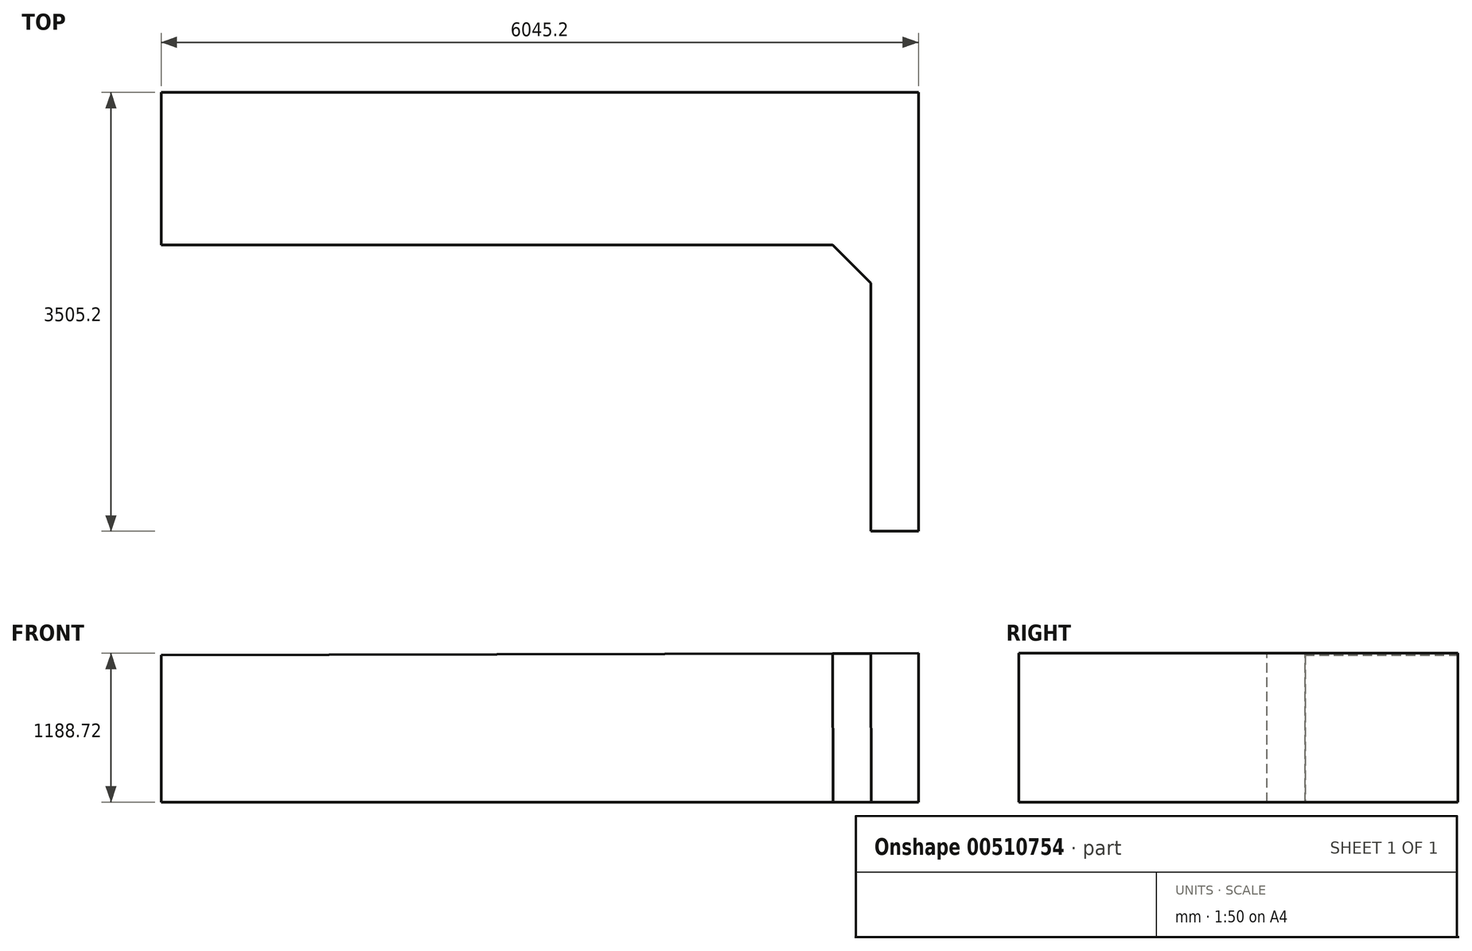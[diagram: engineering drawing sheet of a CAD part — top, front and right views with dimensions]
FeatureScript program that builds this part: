
annotation { "Feature Type Name" : "Feature", "Feature Type Description" : "" }
export const myFeature = defineFeature(function(context is Context, id is Id, definition is map)
    precondition{}
    {
        {
            var Q0;
            Q0=qCreatedBy(makeId("Right.planeOp"),FACE);
            var sketch = newSketch(context, id + "F0", { "sketchPlane" : qUnion([Q0])});
            skLineSegment(sketch, "E0.bottom", {"start": v(0, 295.66) * mm, "end": v(-3505.2, 295.66) * mm});
            skLineSegment(sketch, "E0.top", {"start": v(0, 1484.38) * mm, "end": v(-3505.2, 1484.38) * mm});
            skLineSegment(sketch, "E0.left", {"start": v(0, 295.66) * mm, "end": v(0, 1484.38) * mm});
            skLineSegment(sketch, "E0.right", {"start": v(-3505.2, 295.66) * mm, "end": v(-3505.2, 1484.38) * mm});
            skSolve(sketch);
        }
        {
            var Q0;
            Q0=qCreatedBy(makeId("Right.planeOp"),FACE);
            cPlane(context, id + "F1", {"entities" : qUnion([Q0]), "cplaneType" : CPlaneType.OFFSET, "offset" : 12115.8 * mm, "oppositeDirection" : true, "width" : 152.4 * mm, "height" : 152.4 * mm});
        }
        {
            var Q0;
            Q0=qCreatedBy(id+"F1.planeOp",FACE);
            var sketch = newSketch(context, id + "F2", { "sketchPlane" : qUnion([Q0])});
            skLineSegment(sketch, "E1.bottom", {"start": v(0, 295.66) * mm, "end": v(-3505.2, 295.66) * mm});
            skLineSegment(sketch, "E1.top", {"start": v(0, 1450.85) * mm, "end": v(-3505.2, 1450.85) * mm});
            skLineSegment(sketch, "E1.left", {"start": v(0, 295.66) * mm, "end": v(0, 1450.85) * mm});
            skLineSegment(sketch, "E1.right", {"start": v(-3505.2, 295.66) * mm, "end": v(-3505.2, 1450.85) * mm});
            skSolve(sketch);
        }
        {
            var Q0;
            Q0=makeQuery(id+"F0.imprint","IMPRINT",FACE,{"disambiguationData":[TD([[makeQuery(id+"F0.imprint","IMPRINT",EDGE,{"derivedFrom":sQuery(id+"F0.wireOp",EDGE,"E0.bottom")}),-1.0]])]});
            var Q1;
            Q1=makeQuery(id+"F2.imprint","IMPRINT",FACE,{"disambiguationData":[TD([[makeQuery(id+"F2.imprint","IMPRINT",EDGE,{"derivedFrom":sQuery(id+"F2.wireOp",EDGE,"E1.bottom")}),-1.0]])]});
            loft(context, id + "F3", {"sheetProfilesArray" : [{ "sheetProfileEntities" : qUnion([Q0]) }, { "sheetProfileEntities" : qUnion([Q1]) }]});
        }
        {
            var Q0;
            Q0=makeQuery(id+"F3.opLoft","SWEPT_FACE",FACE,{"disambiguationData":[OSD([sQuery(id+"F0.wireOp",EDGE,"E0.top"),sQuery(id+"F0.wireOp",EDGE,"E0.left"),sQuery(id+"F0.wireOp",EDGE,"E0.right"),sQuery(id+"F2.wireOp",EDGE,"E1.top"),sQuery(id+"F2.wireOp",EDGE,"E1.left"),sQuery(id+"F2.wireOp",EDGE,"E1.right")])]});
            var sketch = newSketch(context, id + "F4", { "sketchPlane" : qUnion([Q0])});
            skLineSegment(sketch, "E2", {"start": v(-11730.74, -3505.2) * mm, "end": v(-11730.74, -1524) * mm});
            skLineSegment(sketch, "E3", {"start": v(-11730.74, -1524) * mm, "end": v(-11425.94, -1219.2) * mm});
            skLineSegment(sketch, "E4", {"start": v(-11425.94, -1219.2) * mm, "end": v(-681.7, -1219.2) * mm});
            skLineSegment(sketch, "E5", {"start": v(-681.7, -1219.2) * mm, "end": v(-376.9, -1524) * mm});
            skLineSegment(sketch, "E6", {"start": v(-376.9, -1524) * mm, "end": v(-376.9, -3505.2) * mm});
            skLineSegment(sketch, "E7", {"start": v(-376.9, -3505.2) * mm, "end": v(-11730.74, -3505.2) * mm});
            skSolve(sketch);
        }
        {
            var Q0;
            Q0 = qSketchRegion(id + "F4", true);
            extrude(context, id + "F5", {"entities" : qUnion([Q0]), "operationType" : NewBodyOperationType.REMOVE, "endBound" : BoundingType.UP_TO_NEXT, "oppositeDirection" : true, "depth" : 30.48 * mm});
        }
        {
            var Q0;
            Q0=qCreatedBy(makeId("Right.planeOp"),FACE);
            cPlane(context, id + "F6", {"entities" : qUnion([Q0]), "cplaneType" : CPlaneType.OFFSET, "offset" : 6045.2 * mm, "oppositeDirection" : true, "width" : 152.4 * mm, "height" : 152.4 * mm});
        }
        {
            var Q0;
            Q0=qCreatedBy(id+"F6.planeOp",FACE);
            var sketch = newSketch(context, id + "F7", { "sketchPlane" : qUnion([Q0])});
            skLineSegment(sketch, "E8.bottom", {"start": v(0, 0) * mm, "end": v(-3505.2, 0) * mm});
            skLineSegment(sketch, "E8.top", {"start": v(0, 1828.8) * mm, "end": v(-3505.2, 1828.8) * mm});
            skLineSegment(sketch, "E8.left", {"start": v(0, 0) * mm, "end": v(0, 1828.8) * mm});
            skLineSegment(sketch, "E8.right", {"start": v(-3505.2, 0) * mm, "end": v(-3505.2, 1828.8) * mm});
            skSolve(sketch);
        }
        {
            var Q0;
            Q0 = qSketchRegion(id + "F7", true);
            extrude(context, id + "F8", {"entities" : qUnion([Q0]), "operationType" : NewBodyOperationType.REMOVE, "endBound" : BoundingType.UP_TO_NEXT, "oppositeDirection" : true, "depth" : 30.48 * mm});
        }
    });
